# Revit family: Plug_Valves-Threaded-Zoeller-5802RTL_5803RTN
name_source: partatom
category: Pipe Accessories
revit_build: Autodesk Revit 2014 (Build: 20130308_1515(x64)
units: mm (PartAtom-declared; Revit-internal decimal feet)

## types (2) — shared parameters
Actuator Mount Base Diameter = 2.492 "
Actuator Mount Diameter = 1.246 "
Assembly Code = D2090800
Bolt Size = 0.625 "
CW Connection = No
CWP (PSI) = 175.00 psi
Description = Rectangular Plug Valve With Bare Stem
Fillet Dim. = 1 "
HW Connection = No
Manufacturer = Zoeller
Material = Metal-Zoeller-Cast Iron
No. of Bolts = 4
Price = Prices may vary. Please consult Manufacturer Representative for most up-to-date price list.
Vent Connection = No
Waste Connection = No
zero-valued in all types: Default Elevation

## per-type parameters (varying)
| type | Actuator Mount Height | Body Dist. From Inlet | Center to Bottom | Center to Top | Flange Diameter | Flange Thickness | Height | Length | Lever Offset Dist. | Model | Nom Dist. | Valve Size | Void Height | Width | Wrench |
| 6030-0082 - 2" | 4.62 " | 0.5 " | 2.875 " | 4.25 " | 3.5 " | 0.691 " | 7.125 " | 5.25 " | 4.25 " | VM-5825R | 0.5 " | 2 " | 3.807 " | 5.25 " | STD : Std |
| 6030-0083 - 3" | 6 " | 0.75 " | 4.63 " | 10 " | 5 " | 0.75 " | 14.63 " | 8.75 " | 7.496 " | VM-5803R | 0.875 " | 3 " | 0.972 " | 8.75 " | VM-3L_Series : 4L |

## geometry (parser evidence)
native form markers: Sweep x7
no freeform markers — native parametric forms only
